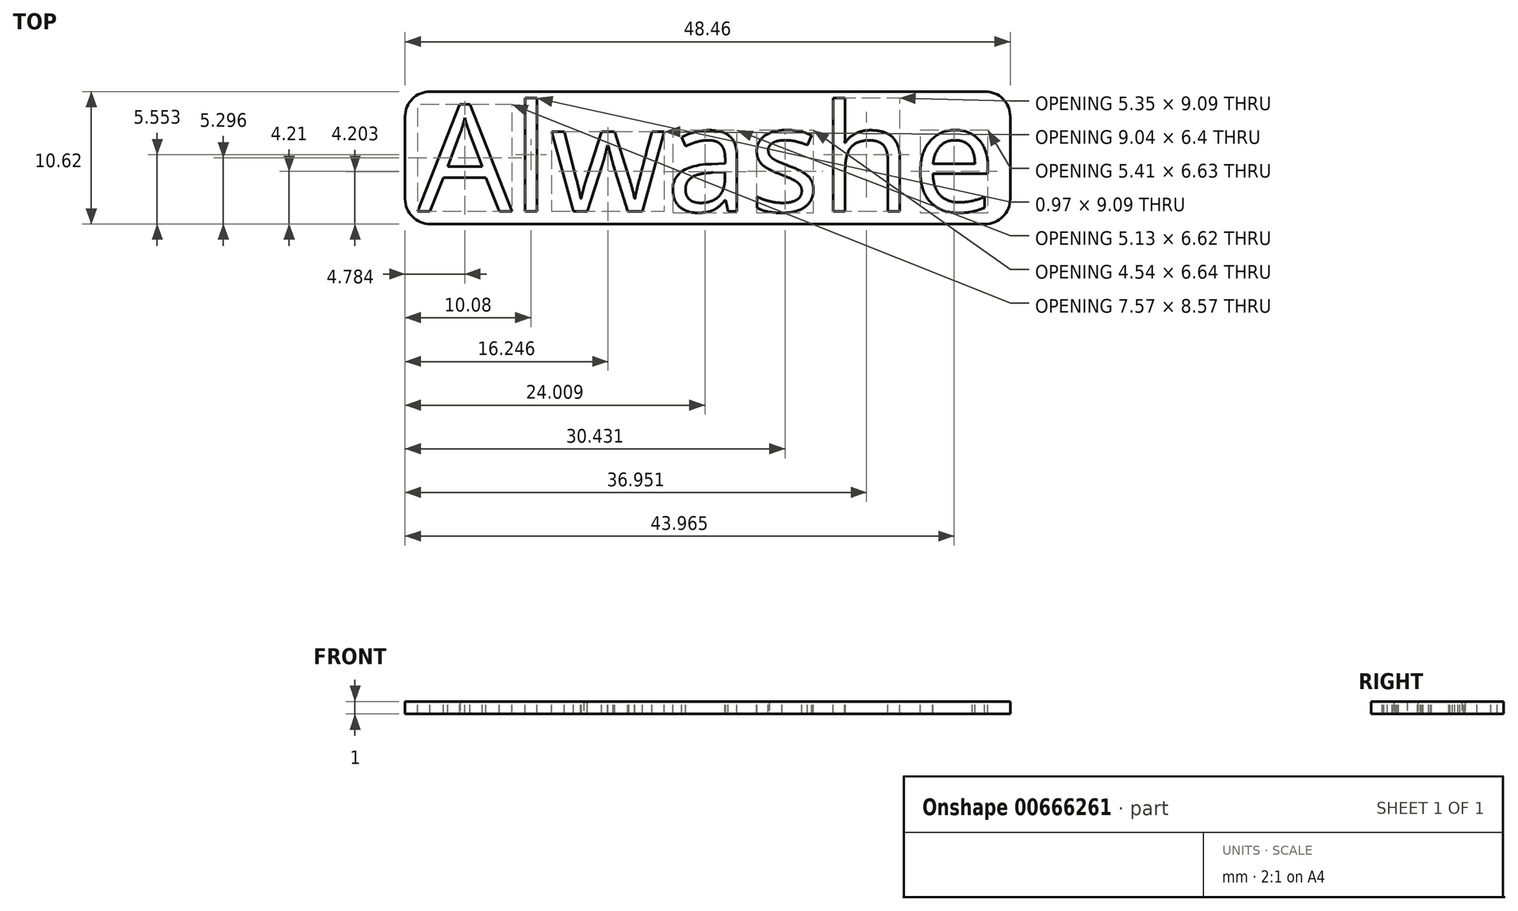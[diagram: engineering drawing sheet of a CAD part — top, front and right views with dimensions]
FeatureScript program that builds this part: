
annotation { "Feature Type Name" : "Feature", "Feature Type Description" : "" }
export const myFeature = defineFeature(function(context is Context, id is Id, definition is map)
    precondition{}
    {
        {
            var Q0;
            Q0=qCreatedBy(makeId("Top.planeOp"),FACE);
            var sketch = newSketch(context, id + "F0", { "sketchPlane" : qUnion([Q0])});
            skText(sketch, "E0", { "text": "Alwashe", "fontName": "OpenSans-Regular.ttf"});
            const initialGuessF0  = {"E0": [-0.02323, -0.0043, 1, 0, 0.00861]};
            skSetInitialGuess(sketch, initialGuessF0);
            skSolve(sketch);
        }
        {
            var Q0;
            Q0=qCreatedBy(makeId("Top.planeOp"),FACE);
            var sketch = newSketch(context, id + "F1", { "sketchPlane" : qUnion([Q0])});
            skLineSegment(sketch, "E1.bottom", {"start": v(22.23, -5.3) * mm, "end": v(-22.23, -5.3) * mm});
            skLineSegment(sketch, "E1.top", {"start": v(22.23, 5.3) * mm, "end": v(-22.23, 5.3) * mm});
            skLineSegment(sketch, "E1.left", {"start": v(24.23, -3.3) * mm, "end": v(24.23, 3.3) * mm});
            skLineSegment(sketch, "E1.right", {"start": v(-24.23, -3.3) * mm, "end": v(-24.23, 3.3) * mm});
            skPoint(sketch, "E1.middle", {"position": v(0, 0) * mm});
            skPoint(sketch, "E2.visualSharp", {"position": v(-24.23, 5.3) * mm});
            skArc(sketch, "E2.filletArc", {"start": v(-22.23, 5.3) * mm, "mid": v(-23.64, 4.72) * mm, "end": v(-24.23, 3.3) * mm});
            skPoint(sketch, "E3.visualSharp", {"position": v(24.23, -5.3) * mm});
            skArc(sketch, "E3.filletArc", {"start": v(22.23, -5.3) * mm, "mid": v(23.64, -4.72) * mm, "end": v(24.23, -3.3) * mm});
            skPoint(sketch, "E4.visualSharp", {"position": v(24.23, 5.3) * mm});
            skArc(sketch, "E4.filletArc", {"start": v(24.23, 3.3) * mm, "mid": v(23.64, 4.72) * mm, "end": v(22.23, 5.3) * mm});
            skPoint(sketch, "E5.visualSharp", {"position": v(-24.23, -5.3) * mm});
            skArc(sketch, "E5.filletArc", {"start": v(-24.23, -3.3) * mm, "mid": v(-23.64, -4.72) * mm, "end": v(-22.23, -5.3) * mm});
            skSolve(sketch);
        }
        {
            var Q0;
            Q0=makeQuery(id+"F1.imprint","IMPRINT",FACE,{"disambiguationData":[TD([[makeQuery(id+"F1.imprint","IMPRINT",EDGE,{"derivedFrom":sQuery(id+"F1.wireOp",EDGE,"E1.bottom")}),-1.0]])]});
            extrude(context, id + "F2", {"entities" : qUnion([Q0]), "oppositeDirection" : true, "depth" : 1 * mm, "offsetDistance" : 25 * mm});
        }
        {
            var Q0;
            Q0 = qSketchRegion(id + "F0", true);
            extrude(context, id + "F3", {"entities" : qUnion([Q0]), "operationType" : NewBodyOperationType.REMOVE, "endBound" : BoundingType.THROUGH_ALL, "oppositeDirection" : true, "depth" : 0.5 * mm, "offsetDistance" : 25 * mm});
        }
    });
